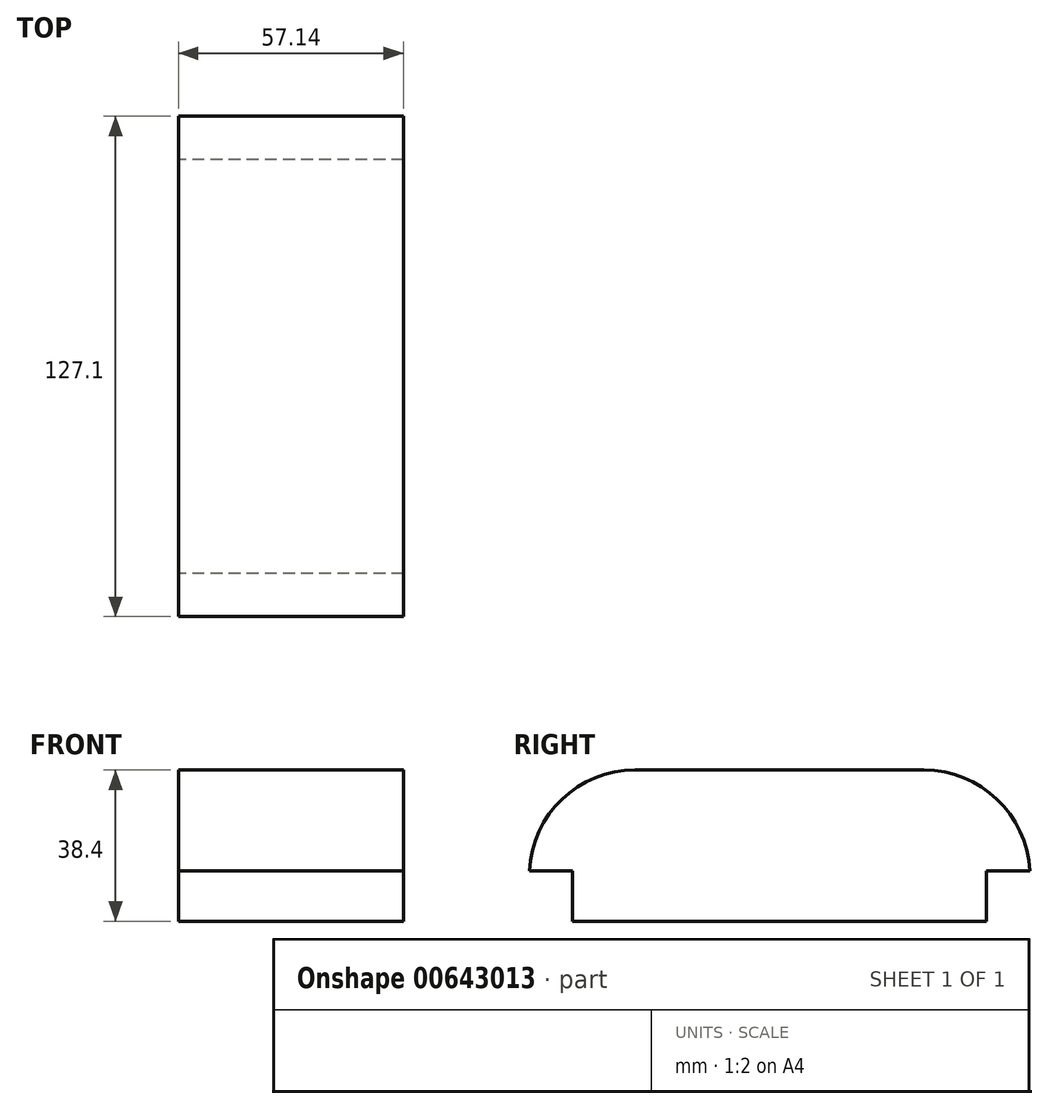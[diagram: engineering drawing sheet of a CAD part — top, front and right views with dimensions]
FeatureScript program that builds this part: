
annotation { "Feature Type Name" : "Feature", "Feature Type Description" : "" }
export const myFeature = defineFeature(function(context is Context, id is Id, definition is map)
    precondition{}
    {
        {
            var Q0;
            Q0=qCreatedBy(makeId("Right.planeOp"),FACE);
            var sketch = newSketch(context, id + "F0", { "sketchPlane" : qUnion([Q0])});
            skLineSegment(sketch, "E0", {"start": v(0, 0) * mm, "end": v(-52.58, 0) * mm});
            skLineSegment(sketch, "E1.MirrorCS", {"start": v(0, 0) * mm, "end": v(52.58, 0) * mm});
            skLineSegment(sketch, "E2", {"start": v(-52.58, 0) * mm, "end": v(-52.58, 12.8) * mm});
            skLineSegment(sketch, "E3.MirrorCS", {"start": v(52.58, 0) * mm, "end": v(52.58, 12.8) * mm});
            skLineSegment(sketch, "E4", {"start": v(-52.58, 12.8) * mm, "end": v(-63.55, 12.8) * mm});
            skLineSegment(sketch, "E5.MirrorCS", {"start": v(52.58, 12.8) * mm, "end": v(63.55, 12.8) * mm});
            skLineSegment(sketch, "E6", {"start": v(-36.73, 38.4) * mm, "end": v(36.73, 38.4) * mm});
            skLineSegment(sketch, "E7", {"start": v(-52.58, 0) * mm, "end": v(-36.73, 0) * mm});
            skPoint(sketch, "E8.orphan", {"position": v(-63.55, 0) * mm});
            skPoint(sketch, "E9.end.orphan", {"position": v(-63.55, 38.4) * mm});
            skArc(sketch, "E10", {"start": v(-36.73, 38.4) * mm, "mid": v(-55.27, 30.98) * mm, "end": v(-63.55, 12.8) * mm});
            skArc(sketch, "E11.MirrorCS", {"start": v(36.73, 38.4) * mm, "mid": v(55.27, 30.98) * mm, "end": v(63.55, 12.8) * mm});
            skPoint(sketch, "E12.MirrorCS.end.orphan", {"position": v(63.55, 38.4) * mm});
            skPoint(sketch, "E12.MirrorCS.start.orphan", {"position": v(63.55, 12.8) * mm});
            skSolve(sketch);
        }
        {
            var Q0;
            Q0=makeQuery(id+"F0.imprint","IMPRINT",FACE,{"disambiguationData":[TD([[makeQuery(id+"F0.imprint","IMPRINT",EDGE,{"derivedFrom":sQuery(id+"F0.wireOp",EDGE,"E0")}),-1.0]])]});
            extrude(context, id + "F1", {"entities" : qUnion([Q0]), "depth" : 28.57 * mm, "offsetDistance" : 25.4 * mm, "hasSecondDirection" : true, "secondDirectionOppositeDirection" : true, "secondDirectionDepth" : 28.57 * mm});
        }
    });
